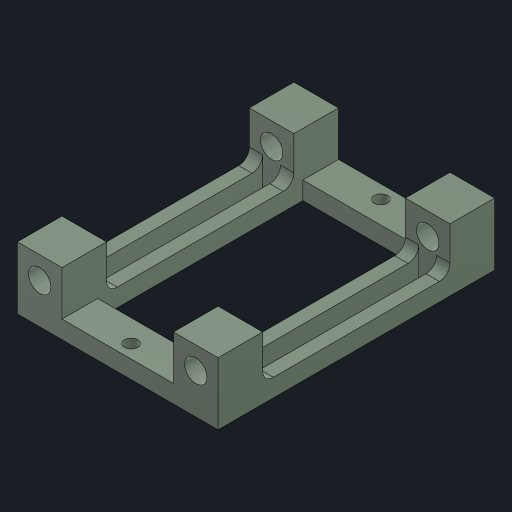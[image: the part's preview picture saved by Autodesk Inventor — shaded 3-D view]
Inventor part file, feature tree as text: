
AUTODESK INVENTOR PART (.ipt)
format: ipt  version: 2023 (Build 270158000, 158)  size: 233,472 bytes
history: native  units: in
note: dims shown in document units (in); Inventor stores cm internally (conversion verified against a paired STEP export)
features: sketch x4, extrude x4, other x3, mirror x2, hole x1, fillet x1, projected_geometry x1
ambient origin geometry x8: Origin, YZ Plane, XZ Plane, XY Plane, X Axis, Y Axis, Z Axis, Center Point
bodies: Body1 (feature_tree)
feature tree (16):
  other  "ソリッド1"
  sketch  "スケッチ1"
  extrude  "押し出し1"  Depth=0.9055in
  hole  "穴1"  [1 undecoded]
  extrude  "押し出し2"  Depth=0.1969in
  extrude  "押し出し5"  Depth=1.1024in
  mirror  "ミラー4"
  extrude  "押し出し6"  Depth=0.315in
  mirror  "ミラー5"
  fillet  "フィレット1"  Radius=0.0787in
  other  "作業平面1"
  other  "作業平面2"
  sketch  "スケッチ2"
  projected_geometry  "投影ループ1"
  sketch  "スケッチ6"
  sketch  "スケッチ7"
note: 1 required parameter value undecoded (feature->parameter linkage not recoverable at this tier; creation-order binding heuristic only, values carry confidence <= 0.55)
